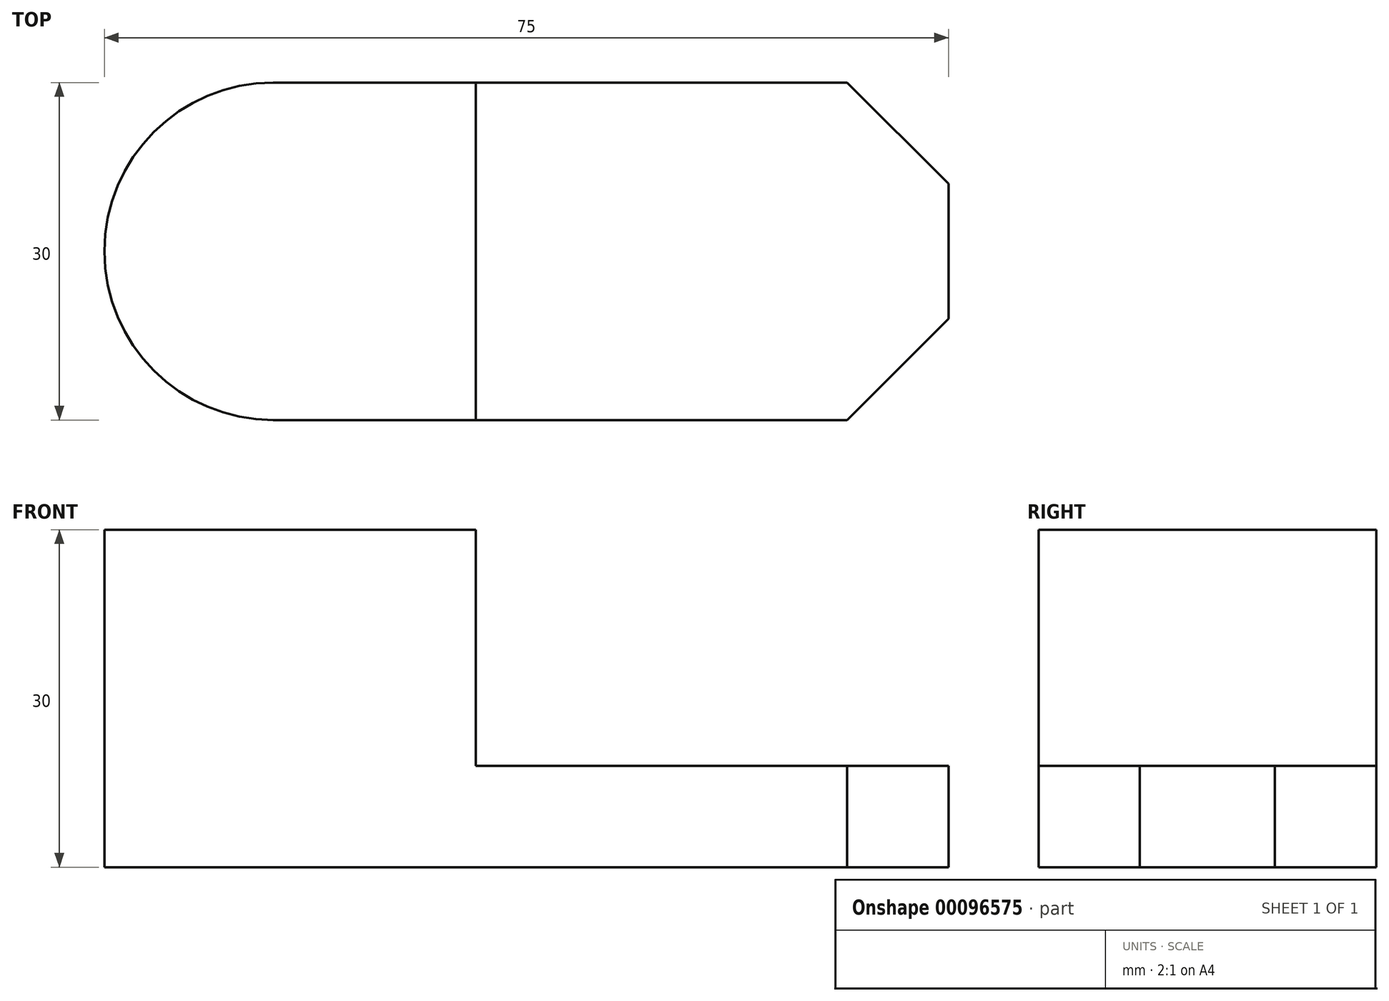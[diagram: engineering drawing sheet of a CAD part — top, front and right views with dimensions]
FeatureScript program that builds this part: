
annotation { "Feature Type Name" : "Feature", "Feature Type Description" : "" }
export const myFeature = defineFeature(function(context is Context, id is Id, definition is map)
    precondition{}
    {
        {
            var Q0;
            Q0=qCreatedBy(makeId("Top.planeOp"),FACE);
            var sketch = newSketch(context, id + "F0", { "sketchPlane" : qUnion([Q0])});
            skArc(sketch, "E0", {"start": v(0, 30) * mm, "mid": v(-15, 15) * mm, "end": v(0, 0) * mm});
            skLineSegment(sketch, "E1", {"start": v(51, 0) * mm, "end": v(60, 9) * mm});
            skLineSegment(sketch, "E2", {"start": v(51, 30) * mm, "end": v(60, 21) * mm});
            skLineSegment(sketch, "E3", {"start": v(60, 9) * mm, "end": v(60, 21) * mm});
            skLineSegment(sketch, "E4", {"start": v(0, 30) * mm, "end": v(51, 30) * mm});
            skLineSegment(sketch, "E5", {"start": v(0, 0) * mm, "end": v(51, 0) * mm});
            skLineSegment(sketch, "E6", {"start": v(18, 30) * mm, "end": v(18, 0) * mm});
            skSolve(sketch);
        }
        {
            var Q0;
            Q0=makeQuery(id+"F0.imprint","IMPRINT",FACE,{"disambiguationData":[TD([[makeQuery(id+"F0.imprint","IMPRINT",EDGE,{"derivedFrom":sQuery(id+"F0.wireOp",EDGE,"E0")}),1.0]])]});
            var Q1;
            {var subQ3=sQuery(id+"F0.wireOp",EDGE,"E1");Q1=makeQuery(id+"F0.imprint","IMPRINT",FACE,{"disambiguationData":[TD([[makeQuery(id+"F0.imprint","IMPRINT",EDGE,{"derivedFrom":subQ3}),1.0]])]});}
            extrude(context, id + "F1", {"entities" : qUnion([Q0, Q1]), "depth" : 9 * mm});
        }
        {
            var Q0;
            {var subQ0=sQuery(id+"F0.wireOp",EDGE,"E0");Q0=makeQuery(id+"F0.imprint","IMPRINT",FACE,{"disambiguationData":[TD([[makeQuery(id+"F0.imprint","IMPRINT",EDGE,{"derivedFrom":subQ0}),1.0]])]});}
            extrude(context, id + "F2", {"entities" : qUnion([Q0]), "operationType" : NewBodyOperationType.ADD, "depth" : 30 * mm});
        }
    });
